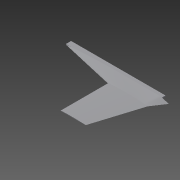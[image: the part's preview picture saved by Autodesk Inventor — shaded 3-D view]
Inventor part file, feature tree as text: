
AUTODESK INVENTOR PART (.ipt)
format: ipt  version: 2014 SP1 (Build 180222100, 222)  size: 199,680 bytes
history: native  units: mm
features: sketch x4, plane x3, loft x2, extrude x1, fillet x1, other x1
ambient origin geometry x8: Origin, YZ Plane, XZ Plane, XY Plane, X Axis, Y Axis, Z Axis, Center Point
bodies: Solid1 (feature_tree)
feature tree (12):
  sketch  "Sketch1"  dims[d0=490.0mm d11=60.0mm]
  plane  "Work Plane1"
  sketch  "Sketch2"  dims[d12=225.0mm d13=120.0mm]
  plane  "Work Plane2"
  loft  "Loft1"
  loft  "Loft2"
  plane  "Work Plane3"
  extrude  "Extrusion2"  TaperAngle=0.0deg  [1 undecoded]
  fillet  "Fillet1"  [1 undecoded]
  sketch  "Sketch3"  dims[d14=0.0mm d15=90.0deg d16=0.0mm d17=90.0deg d18=0.0mm d19=90.0deg]
  other  "Edges1"
  sketch  "Sketch4"  dims[d20=0.0mm d21=90.0deg d22=0.0mm d23=450.0mm d24=2.5mm d25=450.0mm d26=5.0mm d27=450.0mm d28=25.0mm d29=0.0mm d30=40.0mm]
note: 2 required parameter values undecoded (feature->parameter linkage not recoverable at this tier; creation-order binding heuristic only, values carry confidence <= 0.55)
